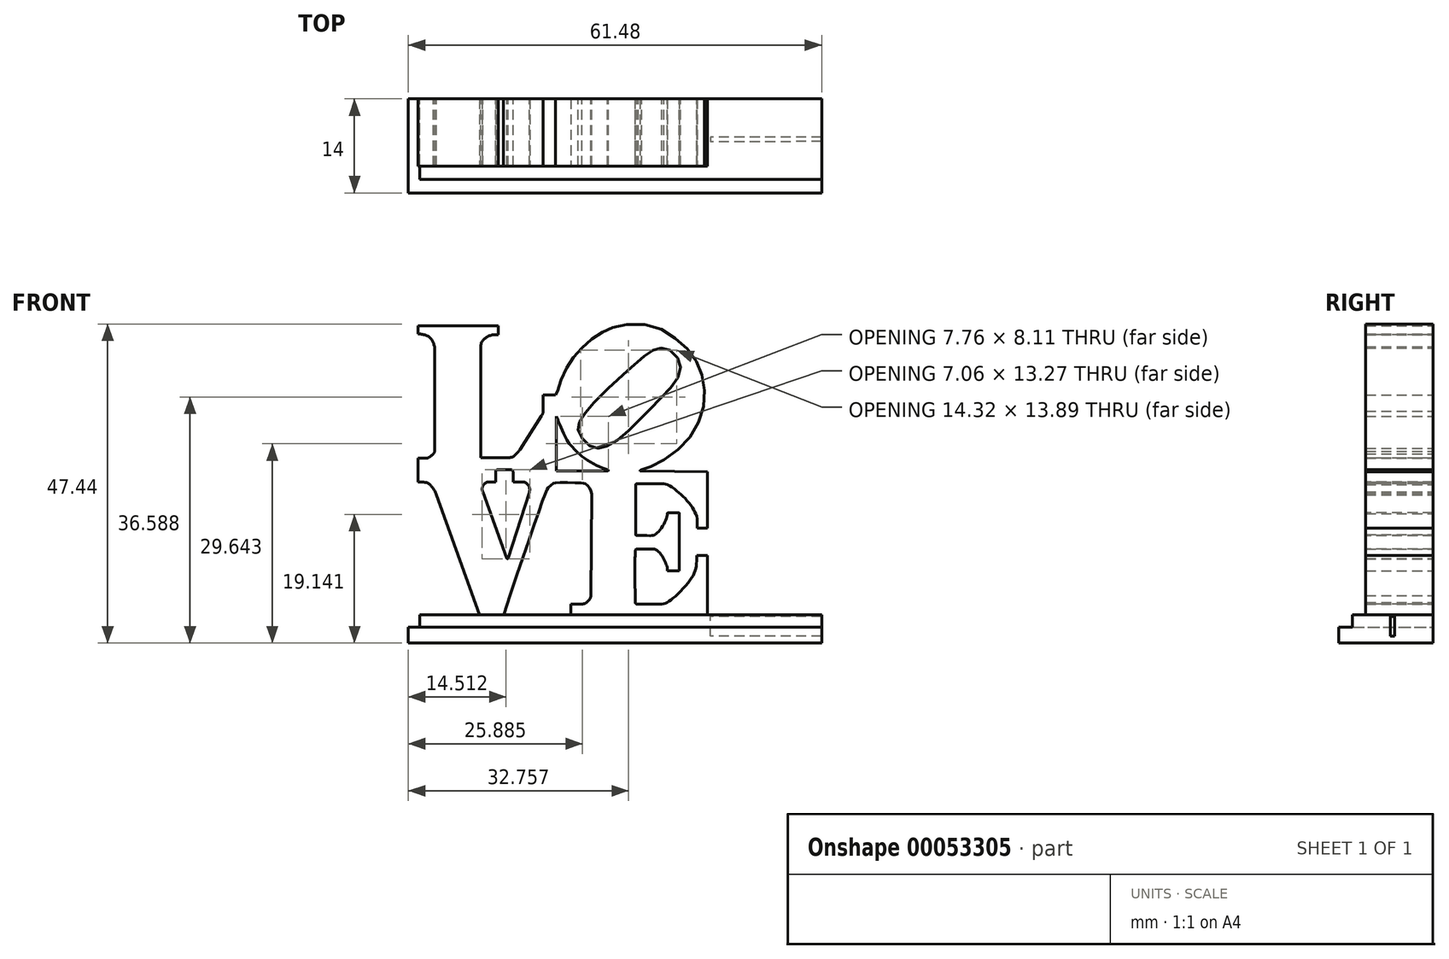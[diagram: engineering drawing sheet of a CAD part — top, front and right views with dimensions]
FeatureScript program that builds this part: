
annotation { "Feature Type Name" : "Feature", "Feature Type Description" : "" }
export const myFeature = defineFeature(function(context is Context, id is Id, definition is map)
    precondition{}
    {
        {
            var Q0;
            Q0=qCreatedBy(makeId("Front.planeOp"),FACE);
            var sketch = newSketch(context, id + "F0", { "sketchPlane" : qUnion([Q0])});
            skLineSegment(sketch, "E0", {"start": v(-19.48, -1.2) * mm, "end": v(-19.48, 14.34) * mm});
            skFitSpline(sketch, "E1", {"points": [v(-19.48, 14.34) * mm, v(-20.3, 15.77) * mm, v(-21.95, 16.25) * mm, v(-22.38, 16.24) * mm], "startDerivative": vector(-1.36, 4.18) * mm, "endDerivative": vector(-1.7, -0.2) * mm});
            skLineSegment(sketch, "E2", {"start": v(-21.95, 16.25) * mm, "end": v(-21.95, 17.47) * mm});
            skLineSegment(sketch, "E3", {"start": v(-21.95, 17.47) * mm, "end": v(-10, 17.47) * mm});
            skLineSegment(sketch, "E4", {"start": v(-10, 17.47) * mm, "end": v(-10, 16.09) * mm});
            skFitSpline(sketch, "E5", {"points": [v(-10, 16.09) * mm, v(-10.84, 16.09) * mm, v(-11.71, 15.77) * mm, v(-12.45, 15.05) * mm, v(-12.65, 14.32) * mm], "startDerivative": vector(-3.46, 0.23) * mm, "endDerivative": vector(-0.46, -3.21) * mm});
            skLineSegment(sketch, "E6", {"start": v(-12.65, 14.32) * mm, "end": v(-12.65, -2.21) * mm});
            skLineSegment(sketch, "E7", {"start": v(-12.65, -2.21) * mm, "end": v(-9.25, -2.21) * mm});
            skFitSpline(sketch, "E8", {"points": [v(-9.25, -2.21) * mm, v(-8.31, -2.16) * mm, v(-7.73, -1.99) * mm, v(-6.88, -1.1) * mm, v(-6.77, -0.96) * mm], "startDerivative": vector(3.41, 0.21) * mm, "endDerivative": vector(0.51, 0.8) * mm});
            skLineSegment(sketch, "E9", {"start": v(-3.58, 4.07) * mm, "end": v(-6.77, -0.96) * mm});
            skFitSpline(sketch, "E10", {"points": [v(-3.58, 4.07) * mm, v(-3.4, 4.42) * mm, v(-3.37, 4.71) * mm], "startDerivative": vector(0.42, 0.66) * mm, "endDerivative": vector(0, 0.64) * mm});
            skLineSegment(sketch, "E11", {"start": v(-3.33, 7.14) * mm, "end": v(-3.37, 4.71) * mm});
            skLineSegment(sketch, "E12", {"start": v(-3.33, 7.14) * mm, "end": v(-1.5, 7.14) * mm});
            skFitSpline(sketch, "E13", {"points": [v(-1.5, 7.14) * mm, v(-1.34, 7.18) * mm, v(-1.23, 7.48) * mm, v(-0.75, 9.22) * mm, v(0.41, 11.66) * mm, v(1.9, 13.61) * mm, v(3.85, 15.44) * mm, v(5.9, 16.69) * mm, v(7.94, 17.44) * mm, v(12.57, 17.5) * mm, v(16.35, 15.57) * mm, v(19.07, 12.8) * mm, v(20.37, 9.62) * mm, v(20.56, 5.74) * mm, v(19.04, 1.69) * mm, v(15.86, -1.63) * mm, v(12.57, -3.55) * mm, v(11.32, -3.93) * mm], "startDerivative": vector(11.77, 0.86) * mm, "endDerivative": vector(-26.73, -6.13) * mm});
            skFitSpline(sketch, "E14", {"points": [v(11.32, -3.93) * mm, v(11.08, -4.1) * mm, v(11.32, -4.17) * mm], "startDerivative": vector(-0.73, -0.38) * mm, "endDerivative": vector(0.76, -0.09) * mm});
            skLineSegment(sketch, "E15", {"start": v(11.32, -4.17) * mm, "end": v(21.1, -4.26) * mm});
            skLineSegment(sketch, "E16", {"start": v(21.1, -4.26) * mm, "end": v(21.1, -12.65) * mm});
            skLineSegment(sketch, "E17", {"start": v(21.1, -12.65) * mm, "end": v(19.6, -12.65) * mm});
            skFitSpline(sketch, "E18", {"points": [v(19.6, -12.65) * mm, v(19.6, -11.9) * mm, v(19.5, -11) * mm, v(19.18, -10.17) * mm, v(18.68, -9.32) * mm, v(17.85, -8.32) * mm, v(16.98, -7.49) * mm, v(16, -6.7) * mm, v(15.1, -6.17) * mm, v(14.64, -6.06) * mm], "startDerivative": vector(0.09, 7.47) * mm, "endDerivative": vector(-5.45, 0.8) * mm});
            skLineSegment(sketch, "E19", {"start": v(10.65, -6.02) * mm, "end": v(14.64, -6.06) * mm});
            skFitSpline(sketch, "E20", {"points": [v(10.65, -6.02) * mm, v(10.5, -6.05) * mm, v(10.45, -6.18) * mm], "startDerivative": vector(-0.33, 0) * mm, "endDerivative": vector(-0.08, -0.32) * mm});
            skLineSegment(sketch, "E21", {"start": v(10.42, -13.6) * mm, "end": v(10.45, -6.18) * mm});
            skFitSpline(sketch, "E22", {"points": [v(10.42, -13.6) * mm, v(10.45, -13.73) * mm, v(10.62, -13.77) * mm, v(11.05, -13.77) * mm, v(12.15, -13.77) * mm, v(12.85, -13.77) * mm, v(13.05, -13.72) * mm, v(13.34, -13.6) * mm, v(13.68, -13.32) * mm, v(14.1, -12.86) * mm, v(14.49, -12.31) * mm, v(14.8, -11.73) * mm, v(15.03, -11.17) * mm, v(15.12, -10.75) * mm, v(15.12, -10.48) * mm], "startDerivative": vector(0.11, -3.9) * mm, "endDerivative": vector(-0.03, 4.69) * mm});
            skFitSpline(sketch, "E23", {"points": [v(15.12, -10.48) * mm, v(15.16, -10.39) * mm, v(15.27, -10.37) * mm, v(16.82, -10.38) * mm, v(16.91, -10.4) * mm, v(16.93, -10.48) * mm, v(16.93, -10.74) * mm, v(16.93, -11.1) * mm, v(16.9, -18.94) * mm, v(16.9, -19.02) * mm], "startDerivative": vector(0.7, 2.28) * mm, "endDerivative": vector(0.01, -0.61) * mm});
            skLineSegment(sketch, "E24", {"start": v(16.9, -19.02) * mm, "end": v(15.14, -19.02) * mm});
            skFitSpline(sketch, "E25", {"points": [v(15.14, -19.02) * mm, v(15.14, -18.68) * mm, v(14.96, -18.03) * mm, v(14.54, -17.16) * mm, v(14.03, -16.37) * mm, v(13.3, -15.8) * mm, v(12.95, -15.77) * mm, v(10.59, -15.75) * mm], "startDerivative": vector(0.25, 3.5) * mm, "endDerivative": vector(-12.34, 0.17) * mm});
            skFitSpline(sketch, "E26", {"points": [v(10.59, -15.75) * mm, v(10.46, -15.81) * mm, v(10.4, -15.95) * mm, v(10.36, -23.71) * mm], "startDerivative": vector(-1.32, -0.51) * mm, "endDerivative": vector(0.16, -13.66) * mm});
            skFitSpline(sketch, "E27", {"points": [v(10.36, -23.71) * mm, v(10.43, -23.87) * mm, v(10.52, -23.95) * mm, v(10.8, -23.97) * mm], "startDerivative": vector(0.2, -0.54) * mm, "endDerivative": vector(0.79, 0.01) * mm});
            skLineSegment(sketch, "E28", {"start": v(10.8, -23.97) * mm, "end": v(14.3, -23.97) * mm});
            skFitSpline(sketch, "E29", {"points": [v(14.3, -23.97) * mm, v(14.91, -23.8) * mm, v(15.5, -23.44) * mm, v(16.42, -22.7) * mm, v(17.99, -21.07) * mm, v(18.93, -19.8) * mm, v(19.3, -18.84) * mm, v(19.47, -17.87) * mm, v(19.48, -16.73) * mm], "startDerivative": vector(6.73, 1.25) * mm, "endDerivative": vector(-0.17, 9.34) * mm});
            skLineSegment(sketch, "E30", {"start": v(19.48, -16.73) * mm, "end": v(21.08, -16.73) * mm});
            skLineSegment(sketch, "E31", {"start": v(21.08, -16.73) * mm, "end": v(21.08, -25.56) * mm});
            skLineSegment(sketch, "E32", {"start": v(21.08, -25.56) * mm, "end": v(0.8, -25.56) * mm});
            skLineSegment(sketch, "E33", {"start": v(0.8, -25.56) * mm, "end": v(0.8, -23.96) * mm});
            skLineSegment(sketch, "E34", {"start": v(0.8, -23.96) * mm, "end": v(2.4, -23.96) * mm});
            skFitSpline(sketch, "E35", {"points": [v(2.4, -23.96) * mm, v(2.88, -23.86) * mm, v(3.28, -23.58) * mm, v(3.62, -23.17) * mm, v(3.76, -22.67) * mm], "startDerivative": vector(2, 0.26) * mm, "endDerivative": vector(0.36, 2.05) * mm});
            skLineSegment(sketch, "E36", {"start": v(3.76, -22.67) * mm, "end": v(3.87, -7.6) * mm});
            skFitSpline(sketch, "E37", {"points": [v(3.87, -7.6) * mm, v(3.6, -6.77) * mm, v(3.05, -6.15) * mm, v(2.73, -6) * mm, v(2.37, -5.94) * mm, v(-1.28, -5.9) * mm, v(-1.88, -6.04) * mm, v(-2.56, -6.64) * mm, v(-2.9, -7.18) * mm, v(-9.24, -25.57) * mm], "startDerivative": vector(-2.44, 10.88) * mm, "endDerivative": vector(-22.83, -67.66) * mm});
            skLineSegment(sketch, "E38", {"start": v(-9.24, -25.57) * mm, "end": v(-12.82, -25.57) * mm});
            skLineSegment(sketch, "E39", {"start": v(-12.82, -25.57) * mm, "end": v(-19.22, -7.68) * mm});
            skFitSpline(sketch, "E40", {"points": [v(-19.22, -7.68) * mm, v(-19.69, -6.77) * mm, v(-20.26, -6.13) * mm, v(-20.67, -5.9) * mm, v(-21.94, -5.79) * mm], "startDerivative": vector(-1.54, 3.48) * mm, "endDerivative": vector(-4.88, 0.13) * mm});
            skLineSegment(sketch, "E41", {"start": v(-21.94, -5.79) * mm, "end": v(-21.94, -2.24) * mm});
            skFitSpline(sketch, "E42", {"points": [v(-21.94, -2.24) * mm, v(-20.67, -2.24) * mm, v(-20.19, -2.03) * mm, v(-19.66, -1.58) * mm], "startDerivative": vector(3.42, -0.2) * mm, "endDerivative": vector(1.73, 1.6) * mm});
            skFitSpline(sketch, "E43", {"points": [v(-19.66, -1.58) * mm, v(-19.54, -1.42) * mm, v(-19.48, -1.2) * mm], "startDerivative": vector(0.29, 0.3) * mm, "endDerivative": vector(0.08, 0.46) * mm});
            skLineSegment(sketch, "E44", {"start": v(-8.56, -17.16) * mm, "end": v(-5.37, -7.3) * mm});
            skFitSpline(sketch, "E45", {"points": [v(-5.37, -7.3) * mm, v(-5.37, -6.66) * mm, v(-5.58, -6.2) * mm, v(-6.11, -5.84) * mm, v(-6.94, -5.78) * mm, v(-7.81, -5.78) * mm], "startDerivative": vector(0.27, 3.5) * mm, "endDerivative": vector(-3.85, 0.04) * mm});
            skLineSegment(sketch, "E46", {"start": v(-7.81, -5.78) * mm, "end": v(-7.81, -4.33) * mm});
            skFitSpline(sketch, "E47", {"points": [v(-7.81, -4.33) * mm, v(-7.88, -4.06) * mm, v(-8.25, -3.98) * mm, v(-10.16, -3.99) * mm, v(-10.32, -4.03) * mm, v(-10.37, -4.12) * mm, v(-10.39, -4.33) * mm], "startDerivative": vector(-0.23, 2.23) * mm, "endDerivative": vector(0.05, -1.9) * mm});
            skLineSegment(sketch, "E48", {"start": v(-10.39, -4.33) * mm, "end": v(-10.39, -5.8) * mm});
            skFitSpline(sketch, "E49", {"points": [v(-10.39, -5.8) * mm, v(-11.5, -5.8) * mm, v(-11.84, -5.88) * mm, v(-12.12, -6.1) * mm, v(-12.32, -6.4) * mm, v(-12.4, -6.64) * mm, v(-12.4, -7.04) * mm, v(-12.34, -7.25) * mm], "startDerivative": vector(-5.35, 0.16) * mm, "endDerivative": vector(0.77, -1.76) * mm});
            skFitSpline(sketch, "E50", {"points": [v(-8.56, -17.16) * mm, v(-8.65, -17.23) * mm, v(-8.72, -17.16) * mm], "startDerivative": vector(-0.17, -0.2) * mm, "endDerivative": vector(-0.15, 0.2) * mm});
            skLineSegment(sketch, "E51", {"start": v(-8.72, -17.16) * mm, "end": v(-12.34, -7.25) * mm});
            skLineSegment(sketch, "E52", {"start": v(6.29, -4.15) * mm, "end": v(-1.39, -4.15) * mm});
            skLineSegment(sketch, "E53", {"start": v(-1.39, -4.15) * mm, "end": v(-1.39, 3.96) * mm});
            skFitSpline(sketch, "E54", {"points": [v(-1.39, 3.96) * mm, v(-0.98, 2.98) * mm, v(-0.48, 1.8) * mm, v(0.36, 0.18) * mm, v(1.7, -1.3) * mm, v(2.7, -2.17) * mm, v(4, -2.99) * mm, v(5.25, -3.61) * mm, v(6.26, -3.97) * mm], "startDerivative": vector(3.75, -8.93) * mm, "endDerivative": vector(9.16, -2.94) * mm});
            skFitSpline(sketch, "E55", {"points": [v(6.26, -3.97) * mm, v(6.38, -4.06) * mm, v(6.29, -4.15) * mm], "startDerivative": vector(0.32, -0.15) * mm, "endDerivative": vector(-0.27, -0.2) * mm});
            skFitSpline(sketch, "E56", {"points": [v(13.05, 13.8) * mm, v(13.92, 14.08) * mm, v(14.98, 14.05) * mm, v(16.14, 13.3) * mm, v(17, 11.96) * mm, v(17.06, 10.75) * mm, v(16.24, 9.05) * mm, v(14.64, 7.19) * mm, v(12.25, 4.7) * mm, v(10.02, 2.48) * mm, v(7.72, 0.48) * mm, v(6, -0.53) * mm, v(4.99, -0.77) * mm, v(3.9, -0.6) * mm, v(2.79, 0.32) * mm, v(2.03, 1.42) * mm, v(1.84, 2.37) * mm, v(2.15, 3.34) * mm, v(3.18, 4.78) * mm, v(5.67, 7.45) * mm, v(11.7, 12.93) * mm, v(13.05, 13.8) * mm]});
            skLineSegment(sketch, "E57", {"start": v(11.2, -4.16) * mm, "end": v(6.29, -4.15) * mm});
            skLineSegment(sketch, "E58", {"start": v(-8.25, -3.98) * mm, "end": v(-1.39, -3.98) * mm});
            skLineSegment(sketch, "E59", {"start": v(-10.16, -3.99) * mm, "end": v(-21.94, -4.03) * mm});
            skSolve(sketch);
        }
        {
            var Q0;
            {var subQ7=sQuery(id+"F0.wireOp",EDGE,"E0");Q0=makeQuery(id+"F0.imprint","IMPRINT",FACE,{"disambiguationData":[TD([[makeQuery(id+"F0.imprint","IMPRINT",EDGE,{"derivedFrom":subQ7}),-1.0]])]});}
            extrude(context, id + "F1", {"entities" : qUnion([Q0]), "depth" : 10 * mm});
        }
        {
            var Q0;
            Q0=qCreatedBy(makeId("Front.planeOp"),FACE);
            var sketch = newSketch(context, id + "F2", { "sketchPlane" : qUnion([Q0])});
            skLineSegment(sketch, "E60", {"start": v(-21.72, -25.6) * mm, "end": v(-21.72, -27.4) * mm});
            skLineSegment(sketch, "E61", {"start": v(-21.72, -27.4) * mm, "end": v(24.69, -27.4) * mm});
            skLineSegment(sketch, "E62", {"start": v(38.1, -25.6) * mm, "end": v(38.1, -27.4) * mm});
            skLineSegment(sketch, "E63", {"start": v(24.69, -27.4) * mm, "end": v(38.1, -27.4) * mm});
            skLineSegment(sketch, "E64", {"start": v(-21.72, -27.4) * mm, "end": v(-23.4, -27.4) * mm});
            skLineSegment(sketch, "E65", {"start": v(-23.4, -27.4) * mm, "end": v(-23.4, -29.74) * mm});
            skLineSegment(sketch, "E66", {"start": v(-23.4, -29.74) * mm, "end": v(38.1, -29.74) * mm});
            skLineSegment(sketch, "E67", {"start": v(38.1, -29.74) * mm, "end": v(38.1, -27.4) * mm});
            skLineSegment(sketch, "E68", {"start": v(-21.72, -25.6) * mm, "end": v(-21.72, -25.52) * mm});
            skPoint(sketch, "E69.start.orphan", {"position": v(38.1, -25.52) * mm});
            skLineSegment(sketch, "E70", {"start": v(38.1, -25.6) * mm, "end": v(38.1, -25.52) * mm});
            skLineSegment(sketch, "E71", {"start": v(38.1, -25.52) * mm, "end": v(-21.72, -25.52) * mm});
            skSolve(sketch);
        }
        {
            var Q0;
            Q0=makeQuery(id+"F2.imprint","IMPRINT",FACE,{"disambiguationData":[TD([[makeQuery(id+"F2.imprint","IMPRINT",EDGE,{"derivedFrom":sQuery(id+"F2.wireOp",EDGE,"E60")}),1.0]])]});
            extrude(context, id + "F3", {"entities" : qUnion([Q0]), "operationType" : NewBodyOperationType.ADD, "depth" : 12 * mm});
        }
        {
            var Q0;
            Q0=makeQuery(id+"F2.imprint","IMPRINT",FACE,{"disambiguationData":[TD([[makeQuery(id+"F2.imprint","IMPRINT",EDGE,{"derivedFrom":sQuery(id+"F2.wireOp",EDGE,"E61")}),-1.0]])]});
            extrude(context, id + "F4", {"entities" : qUnion([Q0]), "operationType" : NewBodyOperationType.ADD, "depth" : 14 * mm});
        }
        {
            var Q0;
            Q0=makeQuery(id+"F3.opExtrude","SWEPT_FACE",FACE,{"disambiguationData":[OSD([sQuery(id+"F2.wireOp",EDGE,"E71")])]});
            cPlane(context, id + "F5", {"entities" : qUnion([Q0]), "cplaneType" : CPlaneType.OFFSET, "offset" : 0.3 * mm, "oppositeDirection" : true, "width" : 150 * mm, "height" : 150 * mm});
        }
        {
            var Q0;
            Q0=qCreatedBy(id+"F5.planeOp",FACE);
            var sketch = newSketch(context, id + "F6", { "sketchPlane" : qUnion([Q0])});
            skLineSegment(sketch, "E72", {"start": v(38.16, 0) * mm, "end": v(38.16, -12) * mm});
            skLineSegment(sketch, "E73", {"start": v(38.16, -6) * mm, "end": v(38.13, -6) * mm});
            skLineSegment(sketch, "E74", {"start": v(38.13, -6) * mm, "end": v(38.13, -5.68) * mm});
            skLineSegment(sketch, "E75", {"start": v(38.13, -5.68) * mm, "end": v(21.54, -5.68) * mm});
            skLineSegment(sketch, "E76", {"start": v(21.54, -5.68) * mm, "end": v(21.54, -6.4) * mm});
            skLineSegment(sketch, "E77", {"start": v(38.13, -6) * mm, "end": v(38.13, -6.34) * mm});
            skLineSegment(sketch, "E78", {"start": v(38.13, -6.34) * mm, "end": v(21.54, -6.4) * mm});
            skSolve(sketch);
        }
        {
            var Q0;
            Q0 = qSketchRegion(id + "F6", true);
            extrude(context, id + "F7", {"entities" : qUnion([Q0]), "operationType" : NewBodyOperationType.REMOVE, "oppositeDirection" : true, "depth" : 2.9 * mm});
        }
    });
